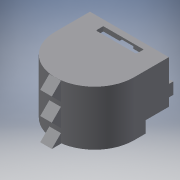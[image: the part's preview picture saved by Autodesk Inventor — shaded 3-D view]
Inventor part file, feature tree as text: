
AUTODESK INVENTOR PART (.ipt)
format: ipt  version: 2016 (Build 200138000, 138)  size: 265,216 bytes
history: native  units: in
note: dims shown in document units (in); Inventor stores cm internally (conversion verified against a paired STEP export)
features: sketch x12, extrude x11, reference x10, projected_geometry x2, plane x1, fillet x1
ambient origin geometry x8: Origin, YZ Plane, XZ Plane, XY Plane, X Axis, Y Axis, Z Axis, Center Point
bodies: Solid1 (feature_tree)
feature tree (37):
  extrude  "Extrusion1"  Depth=0.1969in TaperAngle=0.0deg
  extrude  "Extrusion2"  Depth=0.1969in TaperAngle=0.0deg
  extrude  "Extrusion3"  Depth=0.7874in
  plane  "Work Plane1"
  sketch  "Sketch5"  dims[d11=0.3937in d12=1.9685in d14=0.9774in d15=0.3937in d17=1.0in]
  extrude  "Extrusion5"  Depth=0.3937in
  extrude  "Extrusion6"  Depth=0.197in TaperAngle=0.0deg
  extrude  "Extrusion7"  Depth=2.0in TaperAngle=0.0deg
  extrude  "Extrusion8"  Depth=0.5in
  extrude  "Extrusion9"  Depth=0.5in TaperAngle=0.0deg
  extrude  "Extrusion10"  Depth=0.3937in
  extrude  "Extrusion11"  Depth=0.3937in TaperAngle=0.0deg
  extrude  "Extrusion12"  Depth=0.0394in
  fillet  "Fillet1"  [1 undecoded]
  sketch  "Sketch1"  dims[d0=0.1969in d1=1.5in d2=0.0in]
  reference  "Reference1"
  sketch  "Sketch2"  dims[d3=4.6969in d4=0.0in d5=0.1969in d6=0.0in]
  sketch  "Sketch3"  dims[d9=-1.697in d10=0.7874in]
  sketch  "Sketch6"  dims[d19=0.5in d20=0.0in d21=0.197in d22=0.0in]
  sketch  "Sketch8"  dims[d23=2.0in d24=0.0in d25=2.0in d26=0.0in]
  reference  "Reference3"
  reference  "Reference5"
  reference  "Reference6"
  reference  "Reference7"
  reference  "Reference8"
  sketch  "Sketch9"  dims[d27=16.0in d28=0.0in d29=0.5in]
  reference  "Reference10"
  sketch  "Sketch10"  dims[d30=435.0in d31=0.0in d32=0.5in d33=0.0in]
  reference  "Reference11"
  sketch  "Sketch11"  dims[d34=0.0787in d35=0.3937in]
  sketch  "Sketch12"  dims[d36=0.3937in d37=1.0in d38=0.0in]
  sketch  "Sketch13"  dims[d39=0.0394in d40=0.079in]
  projected_geometry  "Projected Loop1"
  projected_geometry  "Projected Loop2"
  sketch  "Sketch14"
  reference  "Reference12"
  reference  "Reference13"
note: 1 required parameter value undecoded (feature->parameter linkage not recoverable at this tier; creation-order binding heuristic only, values carry confidence <= 0.55)
